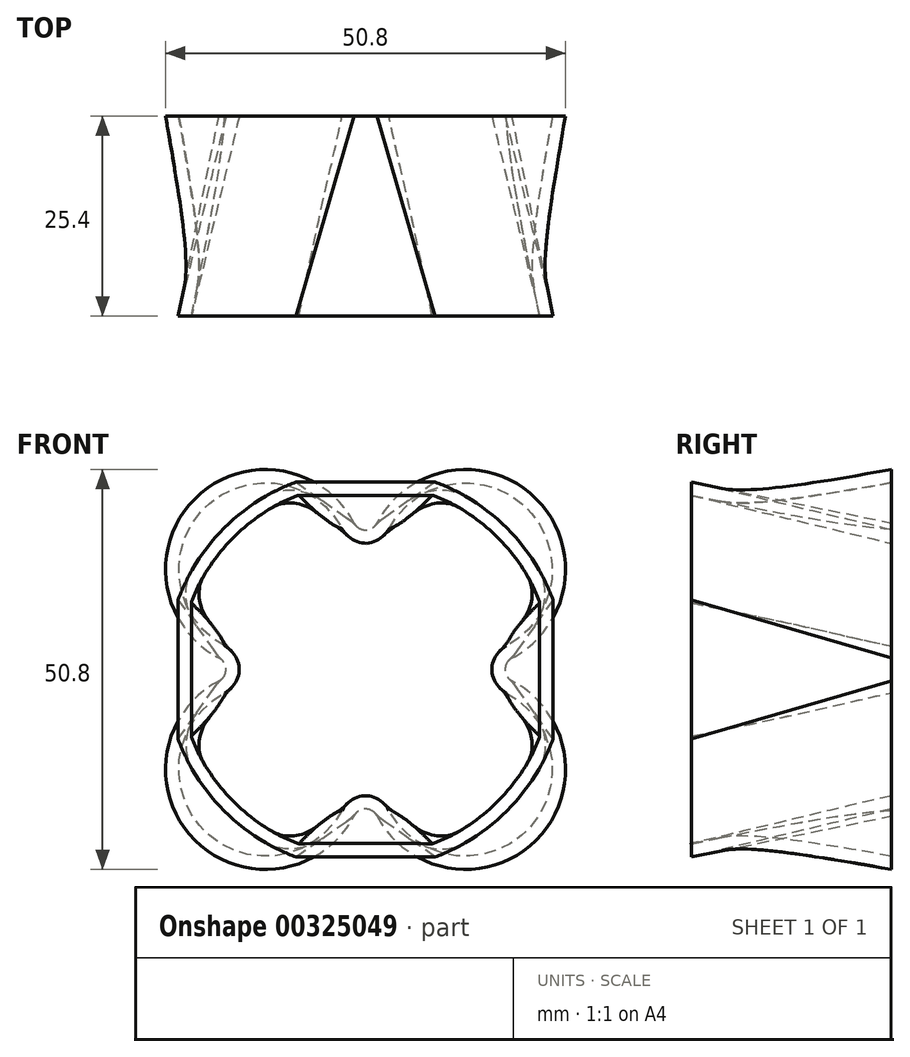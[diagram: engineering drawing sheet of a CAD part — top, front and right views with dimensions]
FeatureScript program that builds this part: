
annotation { "Feature Type Name" : "Feature", "Feature Type Description" : "" }
export const myFeature = defineFeature(function(context is Context, id is Id, definition is map)
    precondition{}
    {
        {
            var Q0;
            Q0=qCreatedBy(makeId("Front.planeOp"),FACE);
            var sketch = newSketch(context, id + "F0", { "sketchPlane" : qUnion([Q0])});
            skArc(sketch, "E0", {"start": v(18.61, 1.46) * mm, "mid": v(21.68, 21.68) * mm, "end": v(1.46, 18.61) * mm});
            skArc(sketch, "E1.1.0", {"start": v(-1.46, 18.61) * mm, "mid": v(-21.68, 21.68) * mm, "end": v(-18.61, 1.46) * mm});
            skArc(sketch, "E1.2.0", {"start": v(-18.61, -1.46) * mm, "mid": v(-21.68, -21.68) * mm, "end": v(-1.46, -18.61) * mm});
            skArc(sketch, "E1.3.0", {"start": v(1.46, -18.61) * mm, "mid": v(21.68, -21.68) * mm, "end": v(18.61, -1.46) * mm});
            skPoint(sketch, "E1.center", {"position": v(0, 0) * mm});
            skPoint(sketch, "E2.visualSharp", {"position": v(0, 12.7) * mm});
            skArc(sketch, "E2.filletArc", {"start": v(-1.46, 18.61) * mm, "mid": v(0, 17.73) * mm, "end": v(1.46, 18.61) * mm});
            skPoint(sketch, "E3.visualSharp", {"position": v(12.7, 0) * mm});
            skArc(sketch, "E3.filletArc", {"start": v(18.61, 1.46) * mm, "mid": v(17.73, 0) * mm, "end": v(18.61, -1.46) * mm});
            skPoint(sketch, "E4.visualSharp", {"position": v(0, -12.7) * mm});
            skArc(sketch, "E4.filletArc", {"start": v(1.46, -18.61) * mm, "mid": v(0, -17.73) * mm, "end": v(-1.46, -18.61) * mm});
            skPoint(sketch, "E5.visualSharp", {"position": v(-12.7, 0) * mm});
            skArc(sketch, "E5.filletArc", {"start": v(-18.61, -1.46) * mm, "mid": v(-17.73, 0) * mm, "end": v(-18.61, 1.46) * mm});
            skSolve(sketch);
        }
        {
            var Q0;
            Q0=qCreatedBy(makeId("Front.planeOp"),FACE);
            cPlane(context, id + "F1", {"entities" : qUnion([Q0]), "cplaneType" : CPlaneType.OFFSET, "offset" : 25.4 * mm, "width" : 152.4 * mm, "height" : 152.4 * mm});
        }
        {
            var Q0;
            Q0=qCreatedBy(id+"F1.planeOp",FACE);
            var sketch = newSketch(context, id + "F2", { "sketchPlane" : qUnion([Q0])});
            skArc(sketch, "E6", {"start": v(-8.84, 23.81) * mm, "mid": v(-17.96, 17.96) * mm, "end": v(-23.81, 8.84) * mm});
            skLineSegment(sketch, "E7.bottom", {"start": v(8.84, 23.81) * mm, "end": v(-8.84, 23.81) * mm});
            skLineSegment(sketch, "E7.top", {"start": v(8.84, -23.81) * mm, "end": v(-8.84, -23.81) * mm});
            skLineSegment(sketch, "E7.left", {"start": v(23.81, 8.84) * mm, "end": v(23.81, -8.84) * mm});
            skLineSegment(sketch, "E7.right", {"start": v(-23.81, 8.84) * mm, "end": v(-23.81, -8.84) * mm});
            skArc(sketch, "E8.trimOffspring", {"start": v(8.84, -23.81) * mm, "mid": v(17.96, -17.96) * mm, "end": v(23.81, -8.84) * mm});
            skArc(sketch, "E9.trimOffspring", {"start": v(23.81, 8.84) * mm, "mid": v(17.96, 17.96) * mm, "end": v(8.84, 23.81) * mm});
            skArc(sketch, "E10.trimOffspring", {"start": v(-23.81, -8.84) * mm, "mid": v(-17.96, -17.96) * mm, "end": v(-8.84, -23.81) * mm});
            skPoint(sketch, "E11.orphan", {"position": v(-23.81, 23.81) * mm});
            skPoint(sketch, "E12.orphan", {"position": v(23.81, 23.81) * mm});
            skPoint(sketch, "E13.orphan", {"position": v(23.81, -23.81) * mm});
            skPoint(sketch, "E14.orphan", {"position": v(-23.81, -23.81) * mm});
            skSolve(sketch);
        }
        {
            var Q0;
            Q0=makeQuery(id+"F2.imprint","IMPRINT",FACE,{"disambiguationData":[TD([[makeQuery(id+"F2.imprint","IMPRINT",EDGE,{"derivedFrom":sQuery(id+"F2.wireOp",EDGE,"E6")}),1.0]])]});
            var Q1;
            Q1=makeQuery(id+"F0.imprint","IMPRINT",FACE,{"disambiguationData":[TD([[makeQuery(id+"F0.imprint","IMPRINT",EDGE,{"derivedFrom":sQuery(id+"F0.wireOp",EDGE,"E0")}),1.0]])]});
            loft(context, id + "F3", {"sheetProfilesArray" : [{ "sheetProfileEntities" : qUnion([Q0]) }, { "sheetProfileEntities" : qUnion([Q1]) }]});
        }
        {
            var Q0;
            Q0=makeQuery(id+"F3.opLoft","CAP_FACE",FACE,{"disambiguationData":[OSD([makeQuery(id+"F2.imprint","IMPRINT",FACE,{"disambiguationData":[TD([[makeQuery(id+"F2.imprint","IMPRINT",EDGE,{"derivedFrom":sQuery(id+"F2.wireOp",EDGE,"E6")}),1.0]])]})])],"isStart":true});
            var Q1;
            Q1=makeQuery(id+"F3.opLoft","CAP_FACE",FACE,{"disambiguationData":[OSD([makeQuery(id+"F0.imprint","IMPRINT",FACE,{"disambiguationData":[TD([[makeQuery(id+"F0.imprint","IMPRINT",EDGE,{"derivedFrom":sQuery(id+"F0.wireOp",EDGE,"E0")}),1.0]])]})])],"isStart":true});
            shell(context, id + "F4", {"entities" : qUnion([Q0, Q1]), "thickness" : 1.65 * mm});
        }
    });
